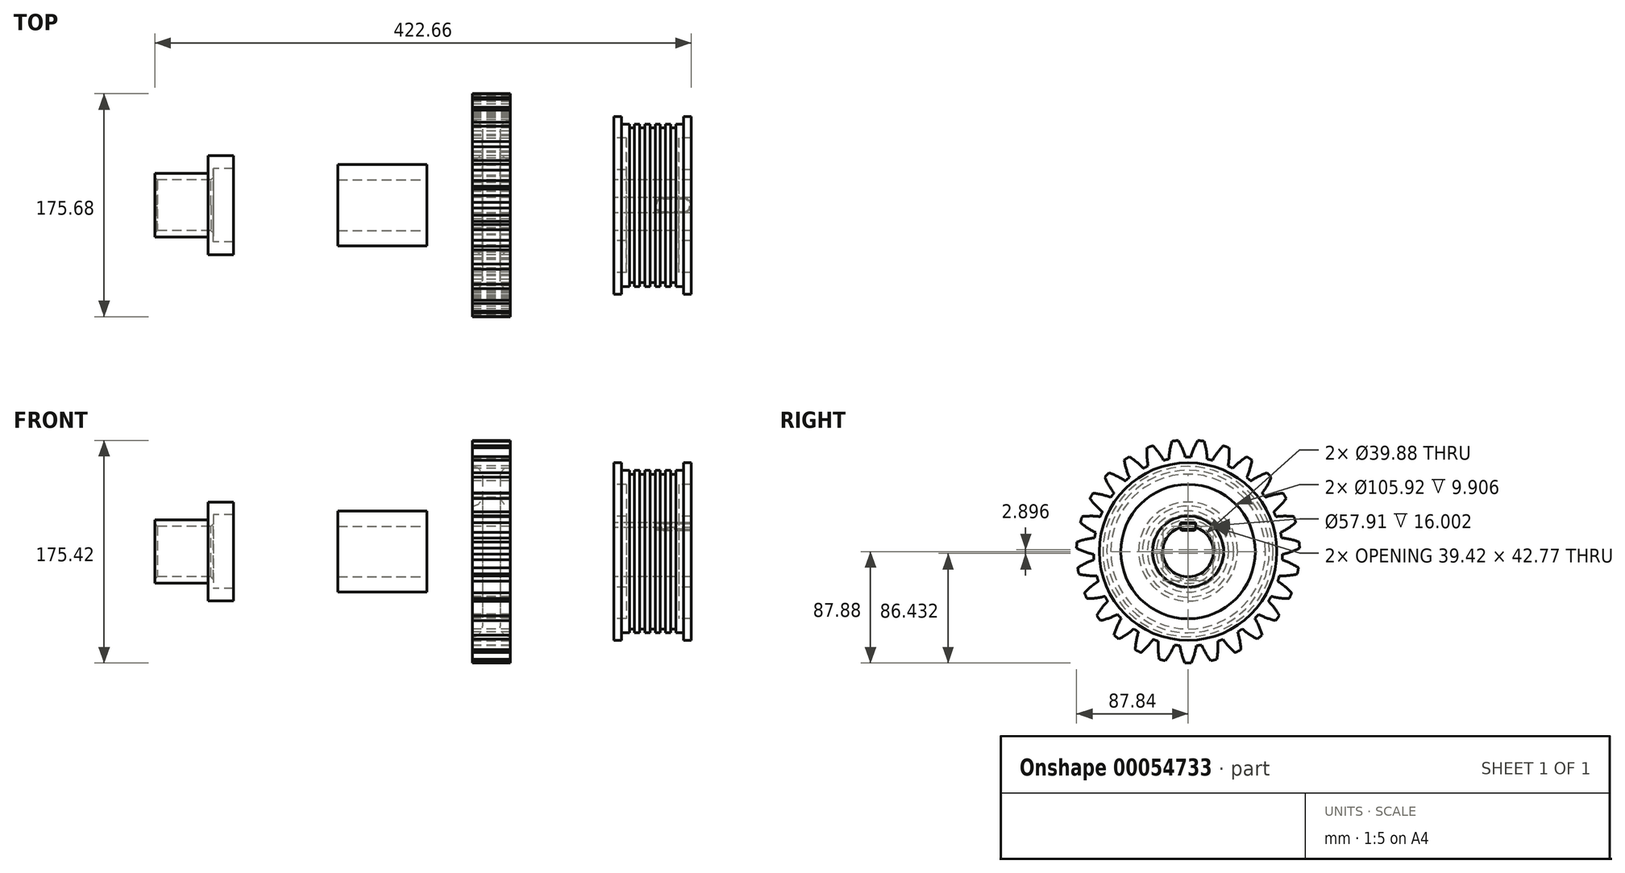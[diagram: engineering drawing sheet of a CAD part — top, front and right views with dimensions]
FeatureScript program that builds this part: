
annotation { "Feature Type Name" : "Feature", "Feature Type Description" : "" }
export const myFeature = defineFeature(function(context is Context, id is Id, definition is map)
    precondition{}
    {
        {
            var Q0;
            Q0=qCreatedBy(makeId("Front.planeOp"),FACE);
            var sketch = newSketch(context, id + "F0", { "sketchPlane" : qUnion([Q0])});
            skLineSegment(sketch, "E0", {"start": v(-30.48, 52.96) * mm, "end": v(-30.48, 69.98) * mm});
            skLineSegment(sketch, "E1", {"start": v(-30.48, 69.98) * mm, "end": v(-24.38, 69.98) * mm});
            skLineSegment(sketch, "E2", {"start": v(-24.38, 69.98) * mm, "end": v(-24.38, 64) * mm});
            skLineSegment(sketch, "E3", {"start": v(-24.38, 64) * mm, "end": v(-18.29, 64) * mm});
            skLineSegment(sketch, "E4", {"start": v(-18.29, 64) * mm, "end": v(-18.29, 60.96) * mm});
            skLineSegment(sketch, "E5", {"start": v(-18.29, 60.96) * mm, "end": v(-14.22, 60.96) * mm});
            skLineSegment(sketch, "E6", {"start": v(-14.22, 60.96) * mm, "end": v(-14.22, 64) * mm});
            skLineSegment(sketch, "E7", {"start": v(-14.22, 64) * mm, "end": v(-10.16, 64) * mm});
            skLineSegment(sketch, "E8", {"start": v(-10.16, 64) * mm, "end": v(-10.16, 60.96) * mm});
            skLineSegment(sketch, "E9", {"start": v(-10.16, 60.96) * mm, "end": v(-6.1, 60.96) * mm});
            skLineSegment(sketch, "E10", {"start": v(-6.1, 60.96) * mm, "end": v(-6.1, 64) * mm});
            skLineSegment(sketch, "E11", {"start": v(-6.1, 64) * mm, "end": v(-2.03, 64) * mm});
            skLineSegment(sketch, "E12", {"start": v(-2.03, 64) * mm, "end": v(-2.03, 60.96) * mm});
            skLineSegment(sketch, "E13", {"start": v(-30.48, 52.96) * mm, "end": v(-20.57, 52.96) * mm});
            skLineSegment(sketch, "E14", {"start": v(-20.57, 52.96) * mm, "end": v(-20.57, 27.94) * mm});
            skLineSegment(sketch, "E15", {"start": v(-20.57, 27.94) * mm, "end": v(-30.48, 27.94) * mm});
            skLineSegment(sketch, "E16", {"start": v(-30.48, 27.94) * mm, "end": v(-30.48, 19.94) * mm});
            skLineSegment(sketch, "E17.0.MirrorCS", {"start": v(30.48, 52.96) * mm, "end": v(30.48, 69.98) * mm});
            skLineSegment(sketch, "E17.1.MirrorCS", {"start": v(24.38, 69.98) * mm, "end": v(24.38, 64) * mm});
            skLineSegment(sketch, "E17.2.MirrorCS", {"start": v(30.48, 69.98) * mm, "end": v(24.38, 69.98) * mm});
            skLineSegment(sketch, "E17.3.MirrorCS", {"start": v(18.29, 64) * mm, "end": v(18.29, 60.96) * mm});
            skLineSegment(sketch, "E17.4.MirrorCS", {"start": v(24.38, 64) * mm, "end": v(18.29, 64) * mm});
            skLineSegment(sketch, "E17.5.MirrorCS", {"start": v(14.22, 60.96) * mm, "end": v(14.22, 64) * mm});
            skLineSegment(sketch, "E17.6.MirrorCS", {"start": v(18.29, 60.96) * mm, "end": v(14.22, 60.96) * mm});
            skLineSegment(sketch, "E17.7.MirrorCS", {"start": v(30.48, 27.94) * mm, "end": v(30.48, 19.94) * mm});
            skLineSegment(sketch, "E17.8.MirrorCS", {"start": v(10.16, 64) * mm, "end": v(10.16, 60.96) * mm});
            skLineSegment(sketch, "E17.9.MirrorCS", {"start": v(14.22, 64) * mm, "end": v(10.16, 64) * mm});
            skLineSegment(sketch, "E17.10.MirrorCS", {"start": v(6.1, 60.96) * mm, "end": v(6.1, 64) * mm});
            skLineSegment(sketch, "E17.11.MirrorCS", {"start": v(10.16, 60.96) * mm, "end": v(6.1, 60.96) * mm});
            skLineSegment(sketch, "E17.12.MirrorCS", {"start": v(30.48, 52.96) * mm, "end": v(20.57, 52.96) * mm});
            skLineSegment(sketch, "E17.13.MirrorCS", {"start": v(2.03, 64) * mm, "end": v(2.03, 60.96) * mm});
            skLineSegment(sketch, "E17.14.MirrorCS", {"start": v(20.57, 52.96) * mm, "end": v(20.57, 27.94) * mm});
            skLineSegment(sketch, "E17.15.MirrorCS", {"start": v(6.1, 64) * mm, "end": v(2.03, 64) * mm});
            skLineSegment(sketch, "E17.16.MirrorCS", {"start": v(20.57, 27.94) * mm, "end": v(30.48, 27.94) * mm});
            skLineSegment(sketch, "E18", {"start": v(-30.48, 19.94) * mm, "end": v(30.48, 19.94) * mm});
            skLineSegment(sketch, "E19", {"start": v(-2.03, 60.96) * mm, "end": v(2.03, 60.96) * mm});
            skLineSegment(sketch, "E20", {"start": v(-30.48, 0) * mm, "end": v(30.48, 0) * mm});
            skSolve(sketch);
        }
        {
            var Q0;
            Q0=makeQuery(id+"F0.imprint","IMPRINT",FACE,{"disambiguationData":[TD([[makeQuery(id+"F0.imprint","IMPRINT",EDGE,{"derivedFrom":sQuery(id+"F0.wireOp",EDGE,"E0")}),-1.0]])]});
            var Q1;
            Q1=sQuery(id+"F0.wireOp",EDGE,"E20");
            revolve(context, id + "F1", {"entities" : qUnion([Q0]), "axis" : qUnion([Q1]), "revolveType" : RevolveType.FULL});
        }
        {
            var Q0;
            Q0=makeQuery(id+"F1.opRevolve","SWEPT_FACE",FACE,{"disambiguationData":[OSD([sQuery(id+"F0.wireOp",EDGE,"E16")])]});
            var sketch = newSketch(context, id + "F2", { "sketchPlane" : qUnion([Q0])});
            skLineSegment(sketch, "E21", {"start": v(-5.97, 22.83) * mm, "end": v(-5.97, 19.02) * mm});
            skLineSegment(sketch, "E22.0.MirrorCS", {"start": v(5.97, 22.83) * mm, "end": v(5.97, 19.02) * mm});
            skLineSegment(sketch, "E23", {"start": v(-5.97, 22.83) * mm, "end": v(5.97, 22.83) * mm});
            skArc(sketch, "E24", {"start": v(5.97, 19.02) * mm, "mid": v(0, 19.94) * mm, "end": v(-5.97, 19.02) * mm});
            skSolve(sketch);
        }
        {
            var Q0;
            Q0=makeQuery(id+"F2.imprint","IMPRINT",FACE,{"disambiguationData":[TD([[makeQuery(id+"F2.imprint","IMPRINT",EDGE,{"derivedFrom":sQuery(id+"F2.wireOp",EDGE,"E21")}),1.0]])]});
            extrude(context, id + "F3", {"entities" : qUnion([Q0]), "operationType" : NewBodyOperationType.REMOVE, "oppositeDirection" : true, "depth" : 127 * mm});
        }
        {
            var Q0;
            Q0=qCreatedBy(makeId("Front.planeOp"),FACE);
            var sketch = newSketch(context, id + "F4", { "sketchPlane" : qUnion([Q0])});
            skLineSegment(sketch, "E25.bottom", {"start": v(43.18, 19.94) * mm, "end": v(623.32, 19.94) * mm});
            skLineSegment(sketch, "E25.top", {"start": v(43.18, 0) * mm, "end": v(1083.06, 0) * mm});
            skLineSegment(sketch, "E25.left", {"start": v(43.18, 19.94) * mm, "end": v(43.18, 0) * mm});
            skLineSegment(sketch, "E26", {"start": v(623.32, 19.94) * mm, "end": v(623.32, 28.96) * mm});
            skLineSegment(sketch, "E27", {"start": v(623.32, 28.96) * mm, "end": v(638.3, 28.96) * mm});
            skLineSegment(sketch, "E28", {"start": v(638.3, 28.96) * mm, "end": v(638.3, 19.94) * mm});
            skLineSegment(sketch, "E29", {"start": v(988.31, 19.94) * mm, "end": v(988.31, 28.96) * mm});
            skLineSegment(sketch, "E30", {"start": v(988.31, 28.96) * mm, "end": v(1003.3, 28.96) * mm});
            skLineSegment(sketch, "E31", {"start": v(1003.3, 28.96) * mm, "end": v(1003.3, 19.94) * mm});
            skLineSegment(sketch, "E32.trimOffspring", {"start": v(638.3, 19.94) * mm, "end": v(988.31, 19.94) * mm});
            skLineSegment(sketch, "E33.trimOffspring", {"start": v(1003.3, 19.94) * mm, "end": v(1083.06, 19.94) * mm});
            skLineSegment(sketch, "E34", {"start": v(1083.06, 19.94) * mm, "end": v(1083.06, 0) * mm});
            skSolve(sketch);
        }
        {
            var Q0;
            Q0=makeQuery(id+"F4.imprint","IMPRINT",FACE,{"disambiguationData":[TD([[makeQuery(id+"F4.imprint","IMPRINT",EDGE,{"derivedFrom":sQuery(id+"F4.wireOp",EDGE,"E25.bottom")}),-1.0]])]});
            var Q1;
            Q1=sQuery(id+"F4.wireOp",EDGE,"E25.top");
            revolve(context, id + "F5", {"entities" : qUnion([Q0]), "axis" : qUnion([Q1]), "revolveType" : RevolveType.FULL});
        }
        {
            var Q0;
            Q0=makeQuery(id+"F5.opRevolve","SWEPT_FACE",FACE,{"disambiguationData":[OSD([sQuery(id+"F4.wireOp",EDGE,"E25.left")])]});
            var sketch = newSketch(context, id + "F6", { "sketchPlane" : qUnion([Q0])});
            skLineSegment(sketch, "E35", {"start": v(-5.97, 19.02) * mm, "end": v(-5.97, 16.48) * mm});
            skLineSegment(sketch, "E36.0.MirrorCS", {"start": v(5.97, 19.02) * mm, "end": v(5.97, 16.48) * mm});
            skLineSegment(sketch, "E37", {"start": v(-5.97, 16.48) * mm, "end": v(5.97, 16.48) * mm});
            skArc(sketch, "E38", {"start": v(5.97, 19.02) * mm, "mid": v(0, 19.94) * mm, "end": v(-5.97, 19.02) * mm});
            skSolve(sketch);
        }
        {
            var Q0;
            Q0=makeQuery(id+"F6.imprint","IMPRINT",FACE,{"disambiguationData":[TD([[makeQuery(id+"F6.imprint","IMPRINT",EDGE,{"derivedFrom":sQuery(id+"F6.wireOp",EDGE,"E35")}),1.0]])]});
            extrude(context, id + "F7", {"entities" : qUnion([Q0]), "operationType" : NewBodyOperationType.REMOVE, "oppositeDirection" : true, "depth" : 45.2 * mm});
        }
        {
            var Q0;
            Q0=makeQuery(id+"F5.opRevolve","SWEPT_FACE",FACE,{"disambiguationData":[OSD([sQuery(id+"F4.wireOp",EDGE,"E26")])]});
            cPlane(context, id + "F8", {"entities" : qUnion([Q0]), "cplaneType" : CPlaneType.OFFSET, "offset" : 38.1 * mm, "width" : 152.4 * mm, "height" : 152.4 * mm});
        }
        {
            var Q0;
            Q0=qCreatedBy(id+"F8.planeOp",FACE);
            var sketch = newSketch(context, id + "F9", { "sketchPlane" : qUnion([Q0])});
            skLineSegment(sketch, "E39", {"start": v(-5.97, 19.02) * mm, "end": v(-5.97, 16.48) * mm});
            skLineSegment(sketch, "E40", {"start": v(-5.97, 16.48) * mm, "end": v(5.97, 16.48) * mm});
            skLineSegment(sketch, "E41.0.MirrorCS", {"start": v(5.97, 19.02) * mm, "end": v(5.97, 16.48) * mm});
            skArc(sketch, "E42", {"start": v(5.97, 19.02) * mm, "mid": v(0, 19.94) * mm, "end": v(-5.97, 19.02) * mm});
            skSolve(sketch);
        }
        {
            var Q0;
            Q0=makeQuery(id+"F9.imprint","IMPRINT",FACE,{"disambiguationData":[TD([[makeQuery(id+"F9.imprint","IMPRINT",EDGE,{"derivedFrom":sQuery(id+"F9.wireOp",EDGE,"E39")}),1.0]])]});
            extrude(context, id + "F10", {"entities" : qUnion([Q0]), "operationType" : NewBodyOperationType.REMOVE, "depth" : 39.88 * mm});
        }
        {
            var Q0;
            Q0=makeQuery(id+"F5.opRevolve","SWEPT_EDGE",EDGE,{"disambiguationData":[OSD([sQuery(id+"F4.wireOp",EDGE,"E25.bottom"),sQuery(id+"F4.wireOp",EDGE,"E25.left")])]});
            var Q1;
            Q1=makeQuery(id+"F5.opRevolve","SWEPT_EDGE",EDGE,{"disambiguationData":[OSD([sQuery(id+"F4.wireOp",EDGE,"E33.trimOffspring"),sQuery(id+"F4.wireOp",EDGE,"E34")])]});
            chamfer(context, id + "F11", {"entities" : qUnion([Q0, Q1]), "width" : 2.03 * mm, "tangentPropagation" : true});
        }
        {
            var Q0;
            Q0=makeQuery(id+"F10.boolean.opBoolean","COPY",EDGE,{"derivedFrom":makeQuery(id+"F10.opExtrude","CAP_EDGE",EDGE,{"disambiguationData":[OSD([sQuery(id+"F9.wireOp",EDGE,"E39")])],"isStart":true})});
            var Q1;
            Q1=makeQuery(id+"F10.boolean.opBoolean","COPY",EDGE,{"derivedFrom":makeQuery(id+"F10.opExtrude","CAP_EDGE",EDGE,{"disambiguationData":[OSD([sQuery(id+"F9.wireOp",EDGE,"E41.0.MirrorCS")])],"isStart":true})});
            var Q2;
            Q2=makeQuery(id+"F10.boolean.opBoolean","COPY",EDGE,{"derivedFrom":makeQuery(id+"F10.opExtrude","CAP_EDGE",EDGE,{"disambiguationData":[OSD([sQuery(id+"F9.wireOp",EDGE,"E39")])],"isStart":false})});
            var Q3;
            Q3=makeQuery(id+"F10.boolean.opBoolean","COPY",EDGE,{"derivedFrom":makeQuery(id+"F10.opExtrude","CAP_EDGE",EDGE,{"disambiguationData":[OSD([sQuery(id+"F9.wireOp",EDGE,"E41.0.MirrorCS")])],"isStart":false})});
            var Q4;
            Q4=makeQuery(id+"F7.boolean.opBoolean","COPY",EDGE,{"derivedFrom":makeQuery(id+"F7.opExtrude","CAP_EDGE",EDGE,{"disambiguationData":[OSD([sQuery(id+"F6.wireOp",EDGE,"E35")])],"isStart":false})});
            var Q5;
            Q5=makeQuery(id+"F7.boolean.opBoolean","COPY",EDGE,{"derivedFrom":makeQuery(id+"F7.opExtrude","CAP_EDGE",EDGE,{"disambiguationData":[OSD([sQuery(id+"F6.wireOp",EDGE,"E36.0.MirrorCS")])],"isStart":false})});
            fillet(context, id + "F12", {"entities" : qUnion([Q0, Q1, Q2, Q3, Q4, Q5]), "radius" : 5.97 * mm, "tangentPropagation" : true, "allowEdgeOverflow" : false});
        }
        {
            var Q0;
            Q0=qCreatedBy(makeId("Front.planeOp"),FACE);
            var sketch = newSketch(context, id + "F13", { "sketchPlane" : qUnion([Q0])});
            skLineSegment(sketch, "E43", {"start": v(-127, 87.88) * mm, "end": v(-127, 0) * mm, "construction": true});
            skLineSegment(sketch, "E44", {"start": v(-141.99, 19.94) * mm, "end": v(-141.99, 35.94) * mm});
            skLineSegment(sketch, "E45", {"start": v(-141.99, 35.94) * mm, "end": v(-133.98, 35.94) * mm});
            skLineSegment(sketch, "E46", {"start": v(-133.98, 35.94) * mm, "end": v(-133.98, 67.06) * mm});
            skLineSegment(sketch, "E47", {"start": v(-133.98, 67.06) * mm, "end": v(-141.99, 67.06) * mm});
            skLineSegment(sketch, "E48", {"start": v(-141.99, 67.06) * mm, "end": v(-141.99, 87.88) * mm});
            skLineSegment(sketch, "E49.0.MirrorCS", {"start": v(-112.01, 67.06) * mm, "end": v(-112.01, 87.88) * mm});
            skLineSegment(sketch, "E49.1.MirrorCS", {"start": v(-120.02, 67.06) * mm, "end": v(-112.01, 67.06) * mm});
            skLineSegment(sketch, "E49.2.MirrorCS", {"start": v(-120.02, 35.94) * mm, "end": v(-120.02, 67.06) * mm});
            skLineSegment(sketch, "E49.3.MirrorCS", {"start": v(-112.01, 19.94) * mm, "end": v(-112.01, 35.94) * mm});
            skLineSegment(sketch, "E49.4.MirrorCS", {"start": v(-112.01, 35.94) * mm, "end": v(-120.02, 35.94) * mm});
            skLineSegment(sketch, "E50", {"start": v(-141.99, 19.94) * mm, "end": v(-112.01, 19.94) * mm});
            skLineSegment(sketch, "E51", {"start": v(-141.99, 87.88) * mm, "end": v(-112.01, 87.88) * mm});
            skLineSegment(sketch, "E52", {"start": v(-141.99, 0) * mm, "end": v(-112.01, 0) * mm, "construction": true});
            skSolve(sketch);
        }
        {
            var Q0;
            Q0=makeQuery(id+"F13.imprint","IMPRINT",FACE,{"disambiguationData":[TD([[makeQuery(id+"F13.imprint","IMPRINT",EDGE,{"derivedFrom":sQuery(id+"F13.wireOp",EDGE,"E44")}),-1.0]])]});
            var Q1;
            Q1=sQuery(id+"F13.wireOp",EDGE,"E52");
            revolve(context, id + "F14", {"entities" : qUnion([Q0]), "axis" : qUnion([Q1]), "revolveType" : RevolveType.FULL});
        }
        {
            var Q0;
            Q0=makeQuery(id+"F14.opRevolve","SWEPT_FACE",FACE,{"disambiguationData":[OSD([sQuery(id+"F13.wireOp",EDGE,"E48")])]});
            var sketch = newSketch(context, id + "F15", { "sketchPlane" : qUnion([Q0])});
            skArc(sketch, "E53", {"start": v(-2.16, 74.4) * mm, "mid": v(-4.54, 81.14) * mm, "end": v(-7.75, 87.54) * mm});
            skArc(sketch, "E54.0.MirrorCS", {"start": v(2.16, 74.4) * mm, "mid": v(4.54, 81.14) * mm, "end": v(7.75, 87.54) * mm});
            skArc(sketch, "E55", {"start": v(2.16, 74.4) * mm, "mid": v(0, 74.42) * mm, "end": v(-2.16, 74.4) * mm});
            skArc(sketch, "E56", {"start": v(7.75, 87.54) * mm, "mid": v(0, 87.88) * mm, "end": v(-7.75, 87.54) * mm});
            skSolve(sketch);
        }
        {
            var Q0;
            Q0=makeQuery(id+"F15.imprint","IMPRINT",FACE,{"disambiguationData":[TD([[makeQuery(id+"F15.imprint","IMPRINT",EDGE,{"derivedFrom":sQuery(id+"F15.wireOp",EDGE,"E53")}),-1.0]])]});
            extrude(context, id + "F16", {"entities" : qUnion([Q0]), "oppositeDirection" : true, "depth" : 33.02 * mm});
        }
        {
            var Q0;
            Q0=makeQuery(id+"F16.opExtrude","SWEPT_BODY",BODY,{"disambiguationData":[OSD([sQuery(id+"F15.wireOp",EDGE,"E53"),sQuery(id+"F15.wireOp",EDGE,"E54.0.MirrorCS"),sQuery(id+"F15.wireOp",EDGE,"E55"),sQuery(id+"F15.wireOp",EDGE,"E56")])]});
            var Q1;
            Q1=makeQuery(id+"F14.opRevolve","SWEPT_FACE",FACE,{"disambiguationData":[OSD([sQuery(id+"F13.wireOp",EDGE,"E50")])]});
            circularPattern(context, id + "F17", {"entities" : qUnion([Q0]), "axis" : qUnion([Q1]), "angle" : 13.33 * degree, "instanceCount" : round(27)});
        }
        {
            var Q0;
            Q0=makeQuery(id+"F17.opPattern","COPY",BODY,{"derivedFrom":makeQuery(id+"F16.opExtrude","SWEPT_BODY",BODY,{"disambiguationData":[OSD([sQuery(id+"F15.wireOp",EDGE,"E53"),sQuery(id+"F15.wireOp",EDGE,"E54.0.MirrorCS"),sQuery(id+"F15.wireOp",EDGE,"E55"),sQuery(id+"F15.wireOp",EDGE,"E56")])]}),"instanceName":"26"});
            var Q1;
            Q1=makeQuery(id+"F16.opExtrude","SWEPT_BODY",BODY,{"disambiguationData":[OSD([sQuery(id+"F15.wireOp",EDGE,"E53"),sQuery(id+"F15.wireOp",EDGE,"E54.0.MirrorCS"),sQuery(id+"F15.wireOp",EDGE,"E55"),sQuery(id+"F15.wireOp",EDGE,"E56")])]});
            var Q2;
            Q2=makeQuery(id+"F17.opPattern","COPY",BODY,{"derivedFrom":makeQuery(id+"F16.opExtrude","SWEPT_BODY",BODY,{"disambiguationData":[OSD([sQuery(id+"F15.wireOp",EDGE,"E53"),sQuery(id+"F15.wireOp",EDGE,"E54.0.MirrorCS"),sQuery(id+"F15.wireOp",EDGE,"E55"),sQuery(id+"F15.wireOp",EDGE,"E56")])]}),"instanceName":"1"});
            var Q3;
            Q3=makeQuery(id+"F17.opPattern","COPY",BODY,{"derivedFrom":makeQuery(id+"F16.opExtrude","SWEPT_BODY",BODY,{"disambiguationData":[OSD([sQuery(id+"F15.wireOp",EDGE,"E53"),sQuery(id+"F15.wireOp",EDGE,"E54.0.MirrorCS"),sQuery(id+"F15.wireOp",EDGE,"E55"),sQuery(id+"F15.wireOp",EDGE,"E56")])]}),"instanceName":"2"});
            var Q4;
            Q4=makeQuery(id+"F17.opPattern","COPY",BODY,{"derivedFrom":makeQuery(id+"F16.opExtrude","SWEPT_BODY",BODY,{"disambiguationData":[OSD([sQuery(id+"F15.wireOp",EDGE,"E53"),sQuery(id+"F15.wireOp",EDGE,"E54.0.MirrorCS"),sQuery(id+"F15.wireOp",EDGE,"E55"),sQuery(id+"F15.wireOp",EDGE,"E56")])]}),"instanceName":"3"});
            var Q5;
            Q5=makeQuery(id+"F17.opPattern","COPY",BODY,{"derivedFrom":makeQuery(id+"F16.opExtrude","SWEPT_BODY",BODY,{"disambiguationData":[OSD([sQuery(id+"F15.wireOp",EDGE,"E53"),sQuery(id+"F15.wireOp",EDGE,"E54.0.MirrorCS"),sQuery(id+"F15.wireOp",EDGE,"E55"),sQuery(id+"F15.wireOp",EDGE,"E56")])]}),"instanceName":"4"});
            var Q6;
            Q6=makeQuery(id+"F17.opPattern","COPY",BODY,{"derivedFrom":makeQuery(id+"F16.opExtrude","SWEPT_BODY",BODY,{"disambiguationData":[OSD([sQuery(id+"F15.wireOp",EDGE,"E53"),sQuery(id+"F15.wireOp",EDGE,"E54.0.MirrorCS"),sQuery(id+"F15.wireOp",EDGE,"E55"),sQuery(id+"F15.wireOp",EDGE,"E56")])]}),"instanceName":"5"});
            var Q7;
            Q7=makeQuery(id+"F17.opPattern","COPY",BODY,{"derivedFrom":makeQuery(id+"F16.opExtrude","SWEPT_BODY",BODY,{"disambiguationData":[OSD([sQuery(id+"F15.wireOp",EDGE,"E53"),sQuery(id+"F15.wireOp",EDGE,"E54.0.MirrorCS"),sQuery(id+"F15.wireOp",EDGE,"E55"),sQuery(id+"F15.wireOp",EDGE,"E56")])]}),"instanceName":"6"});
            var Q8;
            Q8=makeQuery(id+"F17.opPattern","COPY",BODY,{"derivedFrom":makeQuery(id+"F16.opExtrude","SWEPT_BODY",BODY,{"disambiguationData":[OSD([sQuery(id+"F15.wireOp",EDGE,"E53"),sQuery(id+"F15.wireOp",EDGE,"E54.0.MirrorCS"),sQuery(id+"F15.wireOp",EDGE,"E55"),sQuery(id+"F15.wireOp",EDGE,"E56")])]}),"instanceName":"7"});
            var Q9;
            Q9=makeQuery(id+"F17.opPattern","COPY",BODY,{"derivedFrom":makeQuery(id+"F16.opExtrude","SWEPT_BODY",BODY,{"disambiguationData":[OSD([sQuery(id+"F15.wireOp",EDGE,"E53"),sQuery(id+"F15.wireOp",EDGE,"E54.0.MirrorCS"),sQuery(id+"F15.wireOp",EDGE,"E55"),sQuery(id+"F15.wireOp",EDGE,"E56")])]}),"instanceName":"8"});
            var Q10;
            Q10=makeQuery(id+"F17.opPattern","COPY",BODY,{"derivedFrom":makeQuery(id+"F16.opExtrude","SWEPT_BODY",BODY,{"disambiguationData":[OSD([sQuery(id+"F15.wireOp",EDGE,"E53"),sQuery(id+"F15.wireOp",EDGE,"E54.0.MirrorCS"),sQuery(id+"F15.wireOp",EDGE,"E55"),sQuery(id+"F15.wireOp",EDGE,"E56")])]}),"instanceName":"25"});
            var Q11;
            Q11=makeQuery(id+"F17.opPattern","COPY",BODY,{"derivedFrom":makeQuery(id+"F16.opExtrude","SWEPT_BODY",BODY,{"disambiguationData":[OSD([sQuery(id+"F15.wireOp",EDGE,"E53"),sQuery(id+"F15.wireOp",EDGE,"E54.0.MirrorCS"),sQuery(id+"F15.wireOp",EDGE,"E55"),sQuery(id+"F15.wireOp",EDGE,"E56")])]}),"instanceName":"9"});
            var Q12;
            Q12=makeQuery(id+"F17.opPattern","COPY",BODY,{"derivedFrom":makeQuery(id+"F16.opExtrude","SWEPT_BODY",BODY,{"disambiguationData":[OSD([sQuery(id+"F15.wireOp",EDGE,"E53"),sQuery(id+"F15.wireOp",EDGE,"E54.0.MirrorCS"),sQuery(id+"F15.wireOp",EDGE,"E55"),sQuery(id+"F15.wireOp",EDGE,"E56")])]}),"instanceName":"10"});
            var Q13;
            Q13=makeQuery(id+"F17.opPattern","COPY",BODY,{"derivedFrom":makeQuery(id+"F16.opExtrude","SWEPT_BODY",BODY,{"disambiguationData":[OSD([sQuery(id+"F15.wireOp",EDGE,"E53"),sQuery(id+"F15.wireOp",EDGE,"E54.0.MirrorCS"),sQuery(id+"F15.wireOp",EDGE,"E55"),sQuery(id+"F15.wireOp",EDGE,"E56")])]}),"instanceName":"11"});
            var Q14;
            Q14=makeQuery(id+"F17.opPattern","COPY",BODY,{"derivedFrom":makeQuery(id+"F16.opExtrude","SWEPT_BODY",BODY,{"disambiguationData":[OSD([sQuery(id+"F15.wireOp",EDGE,"E53"),sQuery(id+"F15.wireOp",EDGE,"E54.0.MirrorCS"),sQuery(id+"F15.wireOp",EDGE,"E55"),sQuery(id+"F15.wireOp",EDGE,"E56")])]}),"instanceName":"12"});
            var Q15;
            Q15=makeQuery(id+"F17.opPattern","COPY",BODY,{"derivedFrom":makeQuery(id+"F16.opExtrude","SWEPT_BODY",BODY,{"disambiguationData":[OSD([sQuery(id+"F15.wireOp",EDGE,"E53"),sQuery(id+"F15.wireOp",EDGE,"E54.0.MirrorCS"),sQuery(id+"F15.wireOp",EDGE,"E55"),sQuery(id+"F15.wireOp",EDGE,"E56")])]}),"instanceName":"13"});
            var Q16;
            Q16=makeQuery(id+"F17.opPattern","COPY",BODY,{"derivedFrom":makeQuery(id+"F16.opExtrude","SWEPT_BODY",BODY,{"disambiguationData":[OSD([sQuery(id+"F15.wireOp",EDGE,"E53"),sQuery(id+"F15.wireOp",EDGE,"E54.0.MirrorCS"),sQuery(id+"F15.wireOp",EDGE,"E55"),sQuery(id+"F15.wireOp",EDGE,"E56")])]}),"instanceName":"14"});
            var Q17;
            Q17=makeQuery(id+"F17.opPattern","COPY",BODY,{"derivedFrom":makeQuery(id+"F16.opExtrude","SWEPT_BODY",BODY,{"disambiguationData":[OSD([sQuery(id+"F15.wireOp",EDGE,"E53"),sQuery(id+"F15.wireOp",EDGE,"E54.0.MirrorCS"),sQuery(id+"F15.wireOp",EDGE,"E55"),sQuery(id+"F15.wireOp",EDGE,"E56")])]}),"instanceName":"15"});
            var Q18;
            Q18=makeQuery(id+"F17.opPattern","COPY",BODY,{"derivedFrom":makeQuery(id+"F16.opExtrude","SWEPT_BODY",BODY,{"disambiguationData":[OSD([sQuery(id+"F15.wireOp",EDGE,"E53"),sQuery(id+"F15.wireOp",EDGE,"E54.0.MirrorCS"),sQuery(id+"F15.wireOp",EDGE,"E55"),sQuery(id+"F15.wireOp",EDGE,"E56")])]}),"instanceName":"16"});
            var Q19;
            Q19=makeQuery(id+"F17.opPattern","COPY",BODY,{"derivedFrom":makeQuery(id+"F16.opExtrude","SWEPT_BODY",BODY,{"disambiguationData":[OSD([sQuery(id+"F15.wireOp",EDGE,"E53"),sQuery(id+"F15.wireOp",EDGE,"E54.0.MirrorCS"),sQuery(id+"F15.wireOp",EDGE,"E55"),sQuery(id+"F15.wireOp",EDGE,"E56")])]}),"instanceName":"17"});
            var Q20;
            Q20=makeQuery(id+"F17.opPattern","COPY",BODY,{"derivedFrom":makeQuery(id+"F16.opExtrude","SWEPT_BODY",BODY,{"disambiguationData":[OSD([sQuery(id+"F15.wireOp",EDGE,"E53"),sQuery(id+"F15.wireOp",EDGE,"E54.0.MirrorCS"),sQuery(id+"F15.wireOp",EDGE,"E55"),sQuery(id+"F15.wireOp",EDGE,"E56")])]}),"instanceName":"18"});
            var Q21;
            Q21=makeQuery(id+"F17.opPattern","COPY",BODY,{"derivedFrom":makeQuery(id+"F16.opExtrude","SWEPT_BODY",BODY,{"disambiguationData":[OSD([sQuery(id+"F15.wireOp",EDGE,"E53"),sQuery(id+"F15.wireOp",EDGE,"E54.0.MirrorCS"),sQuery(id+"F15.wireOp",EDGE,"E55"),sQuery(id+"F15.wireOp",EDGE,"E56")])]}),"instanceName":"19"});
            var Q22;
            Q22=makeQuery(id+"F17.opPattern","COPY",BODY,{"derivedFrom":makeQuery(id+"F16.opExtrude","SWEPT_BODY",BODY,{"disambiguationData":[OSD([sQuery(id+"F15.wireOp",EDGE,"E53"),sQuery(id+"F15.wireOp",EDGE,"E54.0.MirrorCS"),sQuery(id+"F15.wireOp",EDGE,"E55"),sQuery(id+"F15.wireOp",EDGE,"E56")])]}),"instanceName":"20"});
            var Q23;
            Q23=makeQuery(id+"F17.opPattern","COPY",BODY,{"derivedFrom":makeQuery(id+"F16.opExtrude","SWEPT_BODY",BODY,{"disambiguationData":[OSD([sQuery(id+"F15.wireOp",EDGE,"E53"),sQuery(id+"F15.wireOp",EDGE,"E54.0.MirrorCS"),sQuery(id+"F15.wireOp",EDGE,"E55"),sQuery(id+"F15.wireOp",EDGE,"E56")])]}),"instanceName":"21"});
            var Q24;
            Q24=makeQuery(id+"F17.opPattern","COPY",BODY,{"derivedFrom":makeQuery(id+"F16.opExtrude","SWEPT_BODY",BODY,{"disambiguationData":[OSD([sQuery(id+"F15.wireOp",EDGE,"E53"),sQuery(id+"F15.wireOp",EDGE,"E54.0.MirrorCS"),sQuery(id+"F15.wireOp",EDGE,"E55"),sQuery(id+"F15.wireOp",EDGE,"E56")])]}),"instanceName":"22"});
            var Q25;
            Q25=makeQuery(id+"F17.opPattern","COPY",BODY,{"derivedFrom":makeQuery(id+"F16.opExtrude","SWEPT_BODY",BODY,{"disambiguationData":[OSD([sQuery(id+"F15.wireOp",EDGE,"E53"),sQuery(id+"F15.wireOp",EDGE,"E54.0.MirrorCS"),sQuery(id+"F15.wireOp",EDGE,"E55"),sQuery(id+"F15.wireOp",EDGE,"E56")])]}),"instanceName":"23"});
            var Q26;
            Q26=makeQuery(id+"F17.opPattern","COPY",BODY,{"derivedFrom":makeQuery(id+"F16.opExtrude","SWEPT_BODY",BODY,{"disambiguationData":[OSD([sQuery(id+"F15.wireOp",EDGE,"E53"),sQuery(id+"F15.wireOp",EDGE,"E54.0.MirrorCS"),sQuery(id+"F15.wireOp",EDGE,"E55"),sQuery(id+"F15.wireOp",EDGE,"E56")])]}),"instanceName":"24"});
            var Q27;
            Q27=makeQuery(id+"F14.opRevolve","SWEPT_BODY",BODY,{"disambiguationData":[OSD([sQuery(id+"F13.wireOp",EDGE,"E44"),sQuery(id+"F13.wireOp",EDGE,"E45"),sQuery(id+"F13.wireOp",EDGE,"E46"),sQuery(id+"F13.wireOp",EDGE,"E47"),sQuery(id+"F13.wireOp",EDGE,"E48"),sQuery(id+"F13.wireOp",EDGE,"E49.0.MirrorCS"),sQuery(id+"F13.wireOp",EDGE,"E49.1.MirrorCS"),sQuery(id+"F13.wireOp",EDGE,"E49.2.MirrorCS"),sQuery(id+"F13.wireOp",EDGE,"E49.3.MirrorCS"),sQuery(id+"F13.wireOp",EDGE,"E49.4.MirrorCS"),sQuery(id+"F13.wireOp",EDGE,"E50"),sQuery(id+"F13.wireOp",EDGE,"E51")])]});
            booleanBodies(context, id + "F18", {"operationType" : BooleanOperationType.SUBTRACTION, "tools" : qUnion([Q0, Q1, Q2, Q3, Q4, Q5, Q6, Q7, Q8, Q9, Q10, Q11, Q12, Q13, Q14, Q15, Q16, Q17, Q18, Q19, Q20, Q21, Q22, Q23, Q24, Q25, Q26]), "targets" : qUnion([Q27])});
        }
        {
            var Q0;
            Q0=makeQuery(id+"F14.opRevolve","SWEPT_FACE",FACE,{"disambiguationData":[OSD([sQuery(id+"F13.wireOp",EDGE,"E44")])]});
            var sketch = newSketch(context, id + "F19", { "sketchPlane" : qUnion([Q0])});
            skLineSegment(sketch, "E57", {"start": v(-5.97, -19.02) * mm, "end": v(-5.97, -22.83) * mm});
            skLineSegment(sketch, "E58.0.MirrorCS", {"start": v(5.97, -19.02) * mm, "end": v(5.97, -22.83) * mm});
            skLineSegment(sketch, "E59", {"start": v(-5.97, -22.83) * mm, "end": v(5.97, -22.83) * mm});
            skArc(sketch, "E60", {"start": v(-5.97, -19.02) * mm, "mid": v(0, -19.94) * mm, "end": v(5.97, -19.02) * mm});
            skSolve(sketch);
        }
        {
            var Q0;
            Q0=makeQuery(id+"F19.imprint","IMPRINT",FACE,{"disambiguationData":[TD([[makeQuery(id+"F19.imprint","IMPRINT",EDGE,{"derivedFrom":sQuery(id+"F19.wireOp",EDGE,"E57")}),1.0]])]});
            extrude(context, id + "F20", {"entities" : qUnion([Q0]), "operationType" : NewBodyOperationType.REMOVE, "oppositeDirection" : true, "depth" : 33.02 * mm});
        }
        {
            var Q0;
            Q0=makeQuery(id+"F14.opRevolve","SWEPT_EDGE",EDGE,{"disambiguationData":[OSD([sQuery(id+"F13.wireOp",EDGE,"E45"),sQuery(id+"F13.wireOp",EDGE,"E46")])]});
            var Q1;
            Q1=makeQuery(id+"F14.opRevolve","SWEPT_EDGE",EDGE,{"disambiguationData":[OSD([sQuery(id+"F13.wireOp",EDGE,"E46"),sQuery(id+"F13.wireOp",EDGE,"E47")])]});
            var Q2;
            Q2=makeQuery(id+"F14.opRevolve","SWEPT_EDGE",EDGE,{"disambiguationData":[OSD([sQuery(id+"F13.wireOp",EDGE,"E49.2.MirrorCS"),sQuery(id+"F13.wireOp",EDGE,"E49.4.MirrorCS")])]});
            var Q3;
            Q3=makeQuery(id+"F14.opRevolve","SWEPT_EDGE",EDGE,{"disambiguationData":[OSD([sQuery(id+"F13.wireOp",EDGE,"E49.1.MirrorCS"),sQuery(id+"F13.wireOp",EDGE,"E49.2.MirrorCS")])]});
            fillet(context, id + "F21", {"entities" : qUnion([Q0, Q1, Q2, Q3]), "radius" : 8.13 * mm, "tangentPropagation" : true, "allowEdgeOverflow" : false});
        }
        {
            var Q0;
            Q0=qCreatedBy(makeId("Front.planeOp"),FACE);
            var sketch = newSketch(context, id + "F22", { "sketchPlane" : qUnion([Q0])});
            skLineSegment(sketch, "E61.bottom", {"start": v(-247.9, 32) * mm, "end": v(-177.8, 32) * mm});
            skLineSegment(sketch, "E61.top", {"start": v(-247.9, 19.94) * mm, "end": v(-177.8, 19.94) * mm});
            skLineSegment(sketch, "E61.left", {"start": v(-247.9, 32) * mm, "end": v(-247.9, 19.94) * mm});
            skLineSegment(sketch, "E61.right", {"start": v(-177.8, 32) * mm, "end": v(-177.8, 19.94) * mm});
            skLineSegment(sketch, "E62", {"start": v(-177.8, 0) * mm, "end": v(-247.9, 0) * mm, "construction": true});
            skSolve(sketch);
        }
        {
            var Q0;
            Q0=makeQuery(id+"F22.imprint","IMPRINT",FACE,{"disambiguationData":[TD([[makeQuery(id+"F22.imprint","IMPRINT",EDGE,{"derivedFrom":sQuery(id+"F22.wireOp",EDGE,"E61.bottom")}),-1.0]])]});
            var Q1;
            Q1=sQuery(id+"F22.wireOp",EDGE,"E62");
            revolve(context, id + "F23", {"entities" : qUnion([Q0]), "axis" : qUnion([Q1]), "revolveType" : RevolveType.FULL});
        }
        {
            var Q0;
            Q0=qCreatedBy(makeId("Front.planeOp"),FACE);
            var sketch = newSketch(context, id + "F24", { "sketchPlane" : qUnion([Q0])});
            skLineSegment(sketch, "E63", {"start": v(-392.18, 19.94) * mm, "end": v(-392.18, 25.02) * mm});
            skLineSegment(sketch, "E64", {"start": v(-392.18, 25.02) * mm, "end": v(-350.27, 25.02) * mm});
            skLineSegment(sketch, "E65", {"start": v(-350.27, 25.02) * mm, "end": v(-350.27, 38.99) * mm});
            skLineSegment(sketch, "E66", {"start": v(-350.27, 38.99) * mm, "end": v(-330.2, 38.99) * mm});
            skLineSegment(sketch, "E67", {"start": v(-330.2, 38.99) * mm, "end": v(-330.2, 28.96) * mm});
            skLineSegment(sketch, "E68", {"start": v(-346.2, 19.94) * mm, "end": v(-392.18, 19.94) * mm});
            skLineSegment(sketch, "E69", {"start": v(-392.18, 0) * mm, "end": v(-330.2, 0) * mm, "construction": true});
            skLineSegment(sketch, "E70", {"start": v(-330.2, 28.96) * mm, "end": v(-346.2, 28.96) * mm});
            skLineSegment(sketch, "E71", {"start": v(-346.2, 28.96) * mm, "end": v(-346.2, 19.94) * mm});
            skPoint(sketch, "E72.orphan", {"position": v(-330.2, 19.94) * mm});
            skSolve(sketch);
        }
        {
            var Q0;
            Q0=makeQuery(id+"F24.imprint","IMPRINT",FACE,{"disambiguationData":[TD([[makeQuery(id+"F24.imprint","IMPRINT",EDGE,{"derivedFrom":sQuery(id+"F24.wireOp",EDGE,"E63")}),-1.0]])]});
            var Q1;
            Q1=sQuery(id+"F24.wireOp",EDGE,"E69");
            revolve(context, id + "F25", {"entities" : qUnion([Q0]), "axis" : qUnion([Q1]), "revolveType" : RevolveType.FULL});
        }
        {
            var Q0;
            Q0=makeQuery(id+"F25.opRevolve","SWEPT_EDGE",EDGE,{"disambiguationData":[OSD([sQuery(id+"F24.wireOp",EDGE,"E63"),sQuery(id+"F24.wireOp",EDGE,"E68")])]});
            var Q1;
            Q1=makeQuery(id+"F25.opRevolve","SWEPT_EDGE",EDGE,{"disambiguationData":[OSD([sQuery(id+"F24.wireOp",EDGE,"E68"),sQuery(id+"F24.wireOp",EDGE,"E71")])]});
            chamfer(context, id + "F26", {"entities" : qUnion([Q0, Q1]), "width" : 1.9 * mm, "tangentPropagation" : true});
        }
        {
            var Q0;
            Q0=makeQuery(id+"F5.opRevolve","SWEPT_BODY",BODY,{"disambiguationData":[OSD([sQuery(id+"F4.wireOp",EDGE,"E25.bottom"),sQuery(id+"F4.wireOp",EDGE,"E25.top"),sQuery(id+"F4.wireOp",EDGE,"E25.left"),sQuery(id+"F4.wireOp",EDGE,"E26"),sQuery(id+"F4.wireOp",EDGE,"E27"),sQuery(id+"F4.wireOp",EDGE,"E28"),sQuery(id+"F4.wireOp",EDGE,"E29"),sQuery(id+"F4.wireOp",EDGE,"E30"),sQuery(id+"F4.wireOp",EDGE,"E31"),sQuery(id+"F4.wireOp",EDGE,"E32.trimOffspring"),sQuery(id+"F4.wireOp",EDGE,"E33.trimOffspring"),sQuery(id+"F4.wireOp",EDGE,"E34")])]});
            deleteBodies(context, id + "F27", {"entities" : qUnion([Q0])});
        }
        {
            var Q0;
            Q0=makeQuery(id+"F3.boolean.opBoolean","COPY",FACE,{"derivedFrom":makeQuery(id+"F3.opExtrude","SWEPT_FACE",FACE,{"disambiguationData":[OSD([sQuery(id+"F2.wireOp",EDGE,"E23")])]})});
            var sketch = newSketch(context, id + "F28", { "sketchPlane" : qUnion([Q0])});
            skLineSegment(sketch, "E73.0", {"start": v(24.13, 5.97) * mm, "end": v(8.13, 5.97) * mm});
            skLineSegment(sketch, "E74.0", {"start": v(24.13, -5.97) * mm, "end": v(8.13, -5.97) * mm});
            skArc(sketch, "E75", {"start": v(24.13, -5.97) * mm, "mid": v(30.1, 0) * mm, "end": v(24.13, 5.97) * mm});
            skArc(sketch, "E76", {"start": v(8.13, 5.97) * mm, "mid": v(2.16, 0) * mm, "end": v(8.13, -5.97) * mm});
            skSolve(sketch);
        }
        {
            var Q0;
            Q0=makeQuery(id+"F28.imprint","IMPRINT",FACE,{"disambiguationData":[TD([[makeQuery(id+"F28.imprint","IMPRINT",EDGE,{"derivedFrom":sQuery(id+"F28.wireOp",EDGE,"E73.0")}),1.0]])]});
            extrude(context, id + "F29", {"entities" : qUnion([Q0]), "depth" : 6.1 * mm});
        }
        {
            var Q0;
            Q0=makeQuery(id+"F29.opExtrude","CAP_EDGE",EDGE,{"disambiguationData":[OSD([sQuery(id+"F28.wireOp",EDGE,"E73.0")])],"isStart":false});
            var Q1;
            Q1=makeQuery(id+"F29.opExtrude","CAP_EDGE",EDGE,{"disambiguationData":[OSD([sQuery(id+"F28.wireOp",EDGE,"E73.0")])],"isStart":true});
            chamfer(context, id + "F30", {"entities" : qUnion([Q0, Q1]), "width" : 0.76 * mm, "tangentPropagation" : true});
        }
    });
